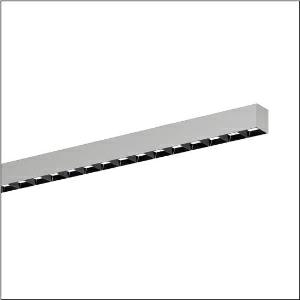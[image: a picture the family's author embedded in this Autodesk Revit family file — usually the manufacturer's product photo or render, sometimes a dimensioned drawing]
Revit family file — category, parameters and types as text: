
# Revit family: silica_r__21_51mx21dc4asb_ccd6
name_source: partatom
category: Lighting Fixtures
units: mm (PartAtom-declared; Revit-internal decimal feet)

## family parameters
Cut with Voids When Loaded = No
Host = Face
Light Source = No
Part Type = Normal
Room Calculation Point = No
Round Connector Dimension = Use Diameter
Shared = No

## types (1)
- --- (1 x LED, 10800 lm, 64.8 W, 4000K)
    Apparent Load = 65 VA
    CIE Flux Codes = 87 99 100 100 100
    Color Rendering = 80
    Color Temperature = 4000K
    Default Elevation = 1800 mm
    Description = Silica® 21, office luminaire, primary light control with darklight reflector, of PMMA, black, CAT 2 (L<= 3000cd/m²), light emission: direct distribution, primary light characteristic: symmetric, installation type: surface-mounted, LED, rated luminous flux: 10.800lm, luminous efficacy: 167lm/W, light colour: 840, colour temperature: 4000K, with terminal, 3+2-pole, max. 2.5mm², mains connection: 220..240V, AC, 50/60Hz, rated input power: 64.8W, luminaire housing, of aluminium, metallic grey (RAL 9006), length: 3.004mm, width: 53mm, height: 53mm, protection rating (complete): IP20, insulation class (complete): insulation class I (protective earthing), certification: CE, permissible operating ambient temperature: 0..+35°C, standard: EN 50419, packaging unit: 1 piece
    Height = 0 mm  [stored 0 ft]
    Lamp = 1 x LED
    Lamp Light Flux = 10800 lm
    Lamp Power = 64.8 W
    Lamp count = 1
    Length = 3004 mm
    Luminous efficacy = 167 lm/W
    Manufacturer = Siteco
    ModVariant = No
    Model = 51MX21DC4ASB
    Mounting Place = Ceiling
    Mounting Type = Recessed
    Number of Poles = 1
    OnlyDefault = Yes
    Power Factor = 1
    Product Name = Silica® 21
    Product group = office luminaire | ceiling recessed
    ProductGroupID = 401
    Protection Class = Protection class I
    Protection Degree = IP 20
    RLX_Detail_Level = 1
    RLX_Emergency_Light_Flux = 0 lm
    RLX_Emergency_Type = 0
    RLX_Emergency_Type_DB = No
    RlxData = <blob elided: 63173 chars, md5=901ea090>
    Socket = socket
    Standby Power = 0 W
    System Light Flux = 10800 lm
    System Power = 65 W
    Type Comments = factory setting: luminous flux: 100 % | dim-lin: 254 | 367 mA
    Type Image = l_1313585.jpg
    URL = http://relux.com
    VarID = @adj_072475
    Voltage = 0 V
    Weight = 0.00 kg
    Width = 53 mm

note: [stored X ft] marks values corroborated as IEEE doubles in the binary element streams (Revit-internal decimal feet)

## geometry (parser evidence)
native form markers: Blend x4, Sweep x9
no freeform markers — native parametric forms only
